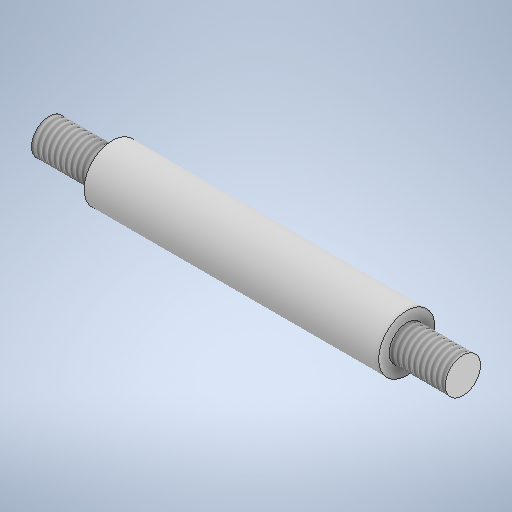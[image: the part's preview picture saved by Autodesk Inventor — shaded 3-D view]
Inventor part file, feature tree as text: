
AUTODESK INVENTOR PART (.ipt)
format: ipt  version: 2025.1 (Build 291241000, 241)  size: 274,432 bytes
history: native  units: mm
features: thread x2, revolve x1, sketch x1
ambient origin geometry x8: Origin, YZ Plane, XZ Plane, XY Plane, X Axis, Y Axis, Z Axis, Center Point
bodies: Solid1 (feature_tree)
feature tree (4):
  revolve  "Revolution1"  [1 undecoded]
  thread  "Thread1"  [1 undecoded]
  thread  "Thread2"  [1 undecoded]
  sketch  "Sketch2"  dims[d0=5.0mm d1=8.0mm d2=9.0mm d3=8.0mm d4=42.0mm d5=90.0deg d6=8.0mm d7=0.0mm d8=11.0mm d9=0.0mm]
note: 3 required parameter values undecoded (feature->parameter linkage not recoverable at this tier; creation-order binding heuristic only, values carry confidence <= 0.55)